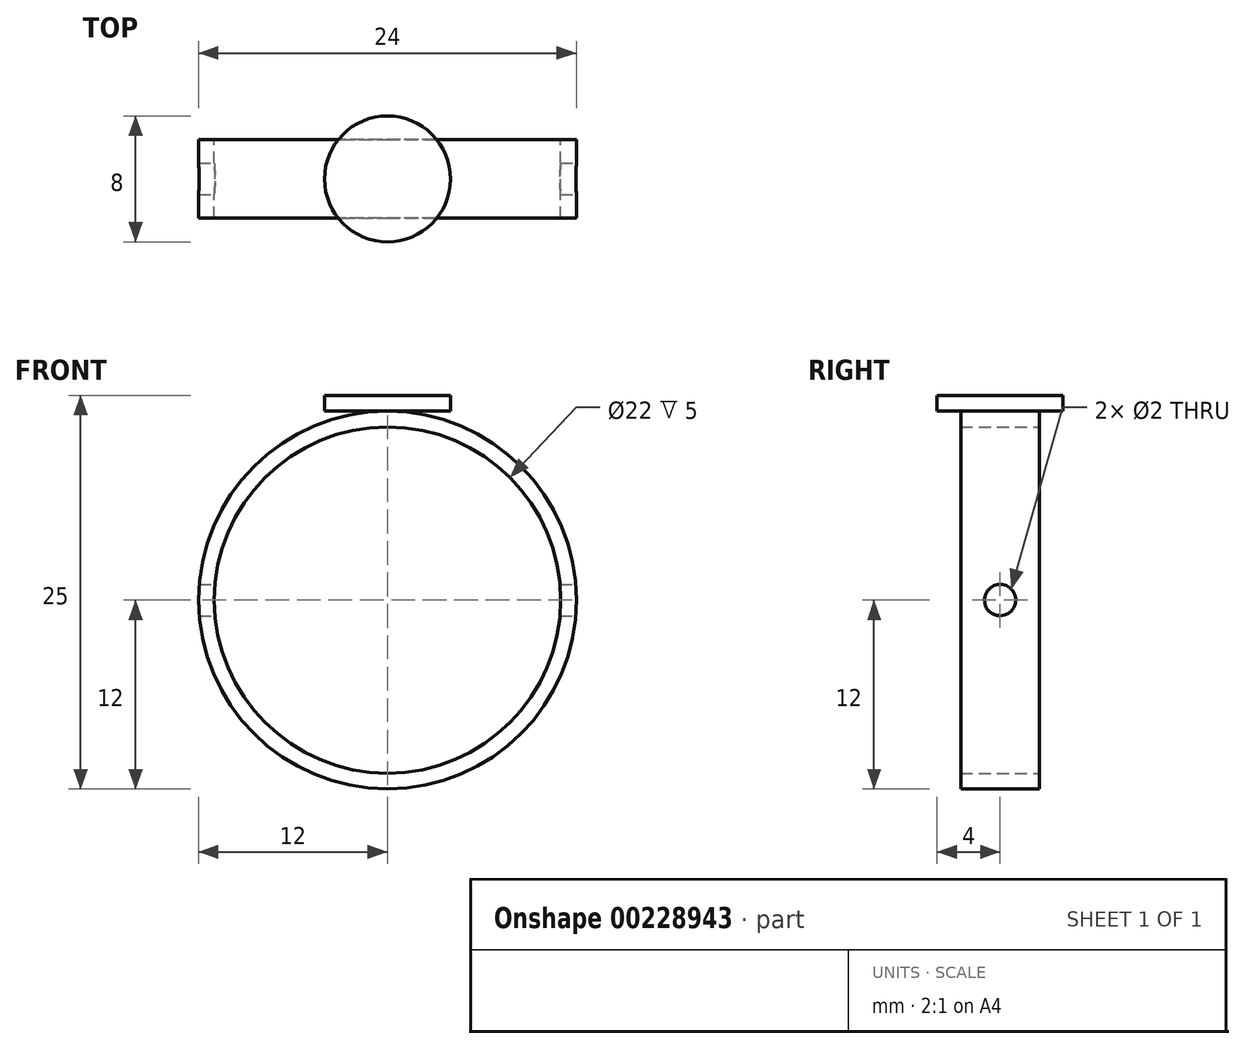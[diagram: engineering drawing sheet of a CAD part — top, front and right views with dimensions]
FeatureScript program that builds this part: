
annotation { "Feature Type Name" : "Feature", "Feature Type Description" : "" }
export const myFeature = defineFeature(function(context is Context, id is Id, definition is map)
    precondition{}
    {
        {
            assignVariable(context, id + "F0", {"name" : "mod", "anyValue" : 1});
        }
        {
            var Q0;
            Q0=qCreatedBy(makeId("Front.planeOp"),FACE);
            var sketch = newSketch(context, id + "F1", { "sketchPlane" : qUnion([Q0])});
            skLineSegment(sketch, "E0", {"start": v(0, 0) * mm, "end": v(0, 11) * mm, "construction": true});
            skCircle(sketch, "E1", {"center": v(0, 0) * mm, "radius": 11 * mm});
            skLineSegment(sketch, "E2", {"start": v(0, 11) * mm, "end": v(0, 12) * mm, "construction": true});
            skCircle(sketch, "E3", {"center": v(0, 0) * mm, "radius": 12 * mm});
            skLineSegment(sketch, "E4.bottom", {"start": v(0, 12) * mm, "end": v(-4, 12) * mm});
            skLineSegment(sketch, "E4.top", {"start": v(0, 13) * mm, "end": v(-4, 13) * mm});
            skLineSegment(sketch, "E4.left", {"start": v(0, 12) * mm, "end": v(0, 13) * mm});
            skLineSegment(sketch, "E4.right", {"start": v(-4, 12) * mm, "end": v(-4, 13) * mm});
            skSolve(sketch);
        }
        {
            var Q0;
            Q0=makeQuery(id+"F1.imprint","IMPRINT",FACE,{"disambiguationData":[TD([[makeQuery(id+"F1.imprint","IMPRINT",EDGE,{"derivedFrom":sQuery(id+"F1.wireOp",EDGE,"E1")}),-1.0]])]});
            extrude(context, id + "F2", {"entities" : qUnion([Q0]), "depth" : (5 * getVariable(context, 'mod')) * mm, "symmetric" : true});
        }
        {
            var Q0;
            Q0=makeQuery(id+"F1.imprint","IMPRINT",FACE,{"disambiguationData":[TD([[makeQuery(id+"F1.imprint","IMPRINT",EDGE,{"derivedFrom":sQuery(id+"F1.wireOp",EDGE,"E4.bottom")}),-1.0]])]});
            var Q1;
            Q1=sQuery(id+"F1.wireOp",EDGE,"E4.left");
            revolve(context, id + "F3", {"operationType" : NewBodyOperationType.ADD, "entities" : qUnion([Q0]), "axis" : qUnion([Q1]), "revolveType" : RevolveType.FULL});
        }
        {
            var Q0;
            Q0=qCreatedBy(makeId("Right.planeOp"),FACE);
            var sketch = newSketch(context, id + "F4", { "sketchPlane" : qUnion([Q0])});
            skCircle(sketch, "E5", {"center": v(0, 0) * mm, "radius": 1 * mm});
            skSolve(sketch);
        }
        {
            var Q0;
            Q0=makeQuery(id+"F4.imprint","IMPRINT",FACE,{"disambiguationData":[TD([[makeQuery(id+"F4.imprint","IMPRINT",EDGE,{"derivedFrom":sQuery(id+"F4.wireOp",EDGE,"E5")}),1.0]])]});
            extrude(context, id + "F5", {"entities" : qUnion([Q0]), "operationType" : NewBodyOperationType.REMOVE, "oppositeDirection" : true, "depth" : 60 * mm, "symmetric" : true});
        }
    });
